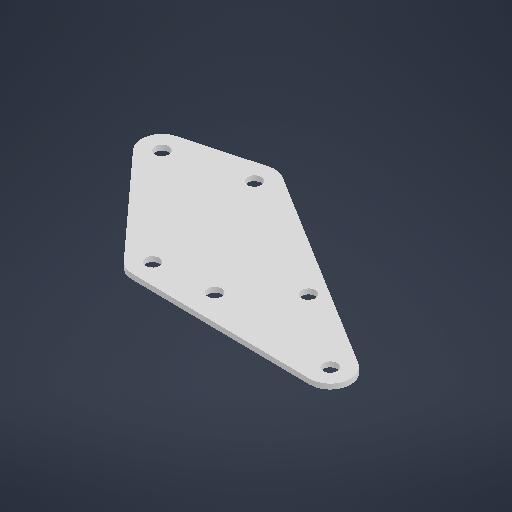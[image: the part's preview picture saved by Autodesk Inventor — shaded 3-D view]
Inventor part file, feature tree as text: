
AUTODESK INVENTOR PART (.ipt)
format: ipt  version: 2025.2 (Build 292293000, 293)  size: 200,704 bytes
history: native  units: in
note: dims shown in document units (in); Inventor stores cm internally (conversion verified against a paired STEP export)
features: extrude x1, sketch x1
ambient origin geometry x8: Origin, YZ Plane, XZ Plane, XY Plane, X Axis, Y Axis, Z Axis, Center Point
bodies: Solid1 (feature_tree)
feature tree (2):
  extrude  "Extrusion1"  Depth=0.0625in
  sketch  "Sketch1"  dims[d0=0.5in d1=0.5in d2=0.5in d8=0.0625in d9=0.0in d10=0.5in]
